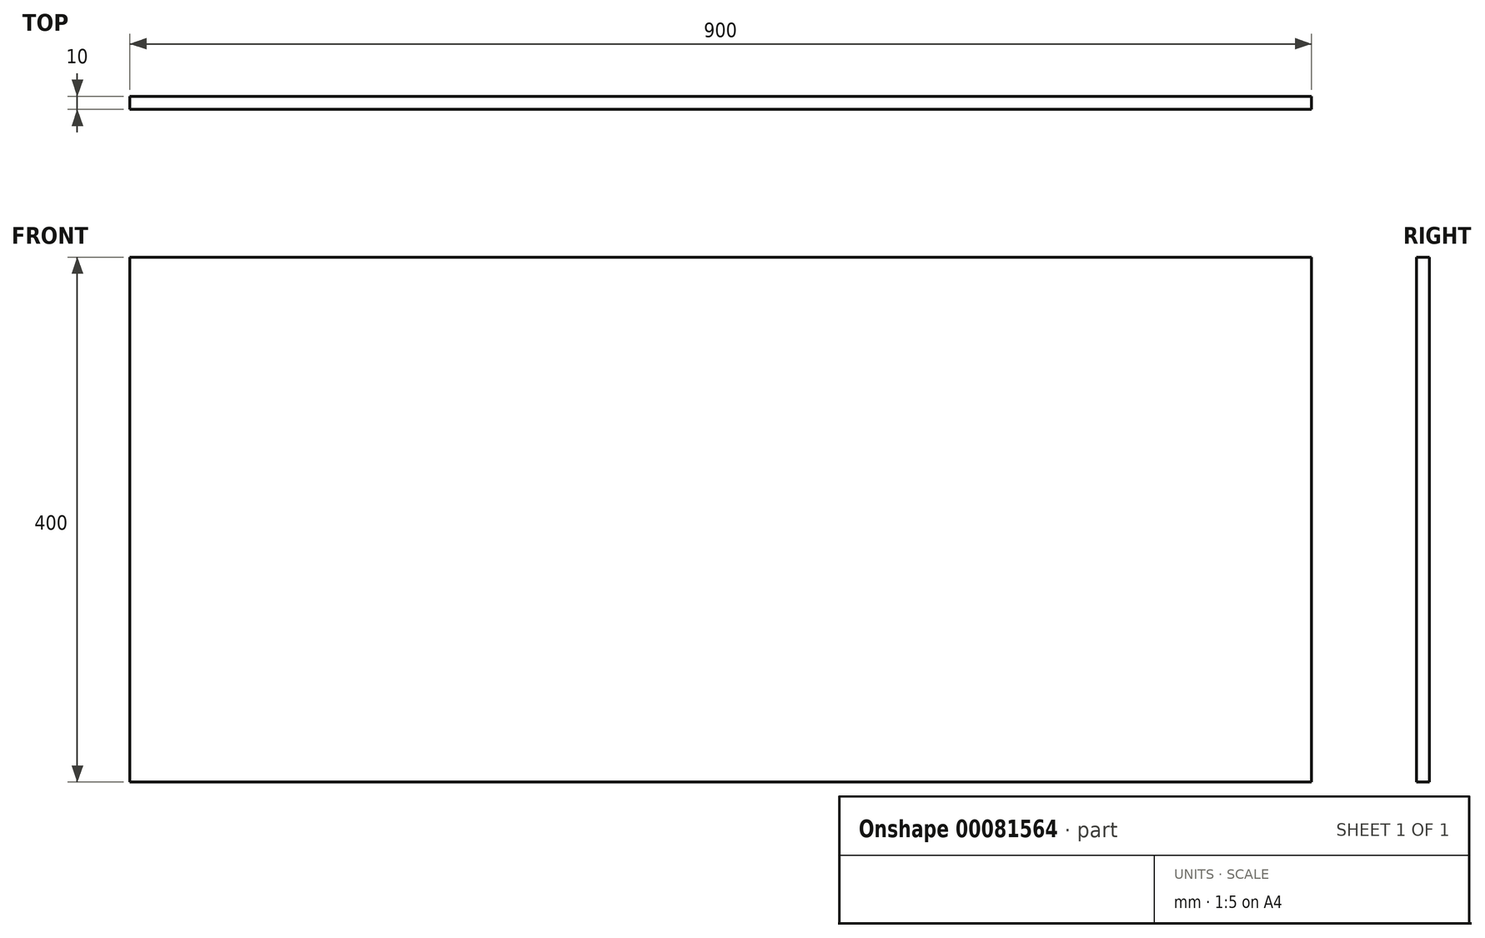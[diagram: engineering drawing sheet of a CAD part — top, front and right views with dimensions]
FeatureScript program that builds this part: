
annotation { "Feature Type Name" : "Feature", "Feature Type Description" : "" }
export const myFeature = defineFeature(function(context is Context, id is Id, definition is map)
    precondition{}
    {
        {
            var Q0;
            Q0=qCreatedBy(makeId("Front.planeOp"),FACE);
            var sketch = newSketch(context, id + "F0", { "sketchPlane" : qUnion([Q0])});
            skLineSegment(sketch, "E0.bottom", {"start": v(-437.07, 62.82) * mm, "end": v(462.93, 62.82) * mm});
            skLineSegment(sketch, "E0.top", {"start": v(-437.07, -337.18) * mm, "end": v(462.93, -337.18) * mm});
            skLineSegment(sketch, "E0.left", {"start": v(-437.07, 62.82) * mm, "end": v(-437.07, -337.18) * mm});
            skLineSegment(sketch, "E0.right", {"start": v(462.93, 62.82) * mm, "end": v(462.93, -337.18) * mm});
            skSolve(sketch);
        }
        {
            var Q0;
            Q0 = qSketchRegion(id + "F0", true);
            extrude(context, id + "F1", {"entities" : qUnion([Q0]), "depth" : 10 * mm});
        }
    });
